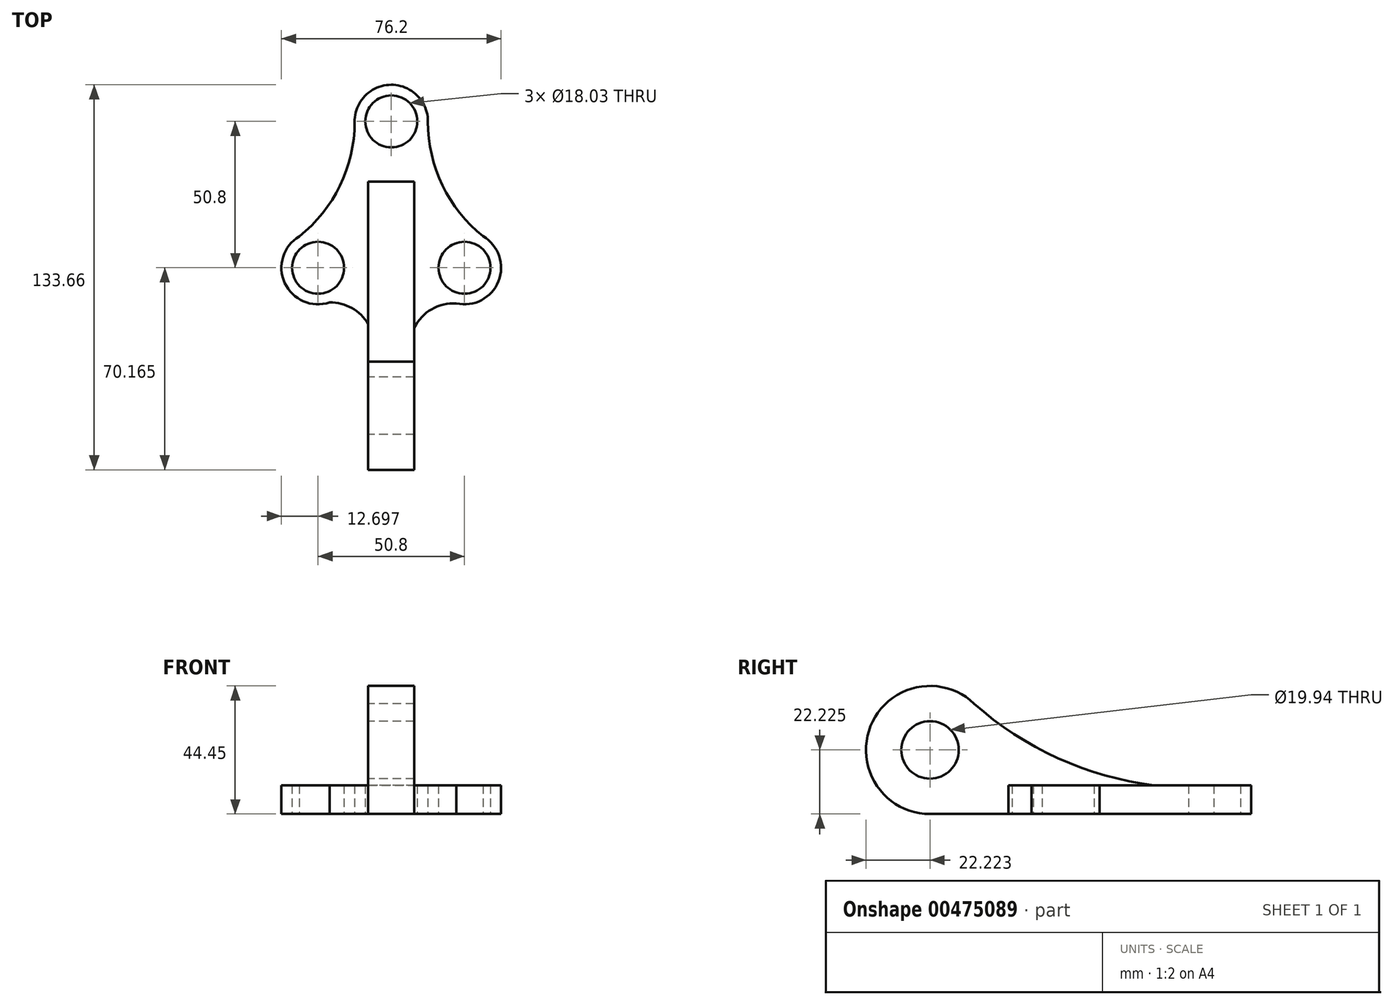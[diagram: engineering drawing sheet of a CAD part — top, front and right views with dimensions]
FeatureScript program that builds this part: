
annotation { "Feature Type Name" : "Feature", "Feature Type Description" : "" }
export const myFeature = defineFeature(function(context is Context, id is Id, definition is map)
    precondition{}
    {
        {
            var Q0;
            Q0=qCreatedBy(makeId("Top.planeOp"),FACE);
            var sketch = newSketch(context, id + "F0", { "sketchPlane" : qUnion([Q0])});
            skCircle(sketch, "E0", {"center": v(-223.53, 109.86) * mm, "radius": 12.7 * mm});
            skCircle(sketch, "E1", {"center": v(-248.93, 59.06) * mm, "radius": 12.7 * mm});
            skCircle(sketch, "E2", {"center": v(-198.13, 59.06) * mm, "radius": 12.7 * mm});
            skPoint(sketch, "E3", {"position": v(-236.23, 110.12) * mm});
            skPoint(sketch, "E4", {"position": v(-210.83, 109.93) * mm});
            skPoint(sketch, "E5", {"position": v(-191.66, 69.98) * mm});
            skArc(sketch, "E6", {"start": v(-210.83, 109.93) * mm, "mid": v(-205.83, 87.76) * mm, "end": v(-191.66, 69.98) * mm});
            skLineSegment(sketch, "E7.bottom", {"start": v(-231.53, 88.9) * mm, "end": v(-215.53, 88.9) * mm});
            skLineSegment(sketch, "E7.top", {"start": v(-231.53, 0) * mm, "end": v(-215.53, 0) * mm});
            skLineSegment(sketch, "E7.left", {"start": v(-231.53, 88.9) * mm, "end": v(-231.53, 0) * mm});
            skLineSegment(sketch, "E7.right", {"start": v(-215.53, 88.9) * mm, "end": v(-215.53, 0) * mm});
            skCircle(sketch, "E8", {"center": v(-248.93, 59.06) * mm, "radius": 9.02 * mm});
            skCircle(sketch, "E9", {"center": v(-198.13, 59.06) * mm, "radius": 9.02 * mm});
            skCircle(sketch, "E10", {"center": v(-223.53, 109.86) * mm, "radius": 9.02 * mm});
            skPoint(sketch, "E11", {"position": v(-257.57, 68.36) * mm});
            skArc(sketch, "E12", {"start": v(-257.57, 68.36) * mm, "mid": v(-241.8, 86.63) * mm, "end": v(-236.23, 110.12) * mm});
            skPoint(sketch, "E13", {"position": v(-198.74, 46.37) * mm});
            skPoint(sketch, "E14", {"position": v(-215.53, 38.26) * mm});
            skPoint(sketch, "E15", {"position": v(-231.53, 39.54) * mm});
            skArc(sketch, "E16", {"start": v(-198.74, 46.37) * mm, "mid": v(-208.52, 45.19) * mm, "end": v(-215.53, 38.26) * mm});
            skPoint(sketch, "E17", {"position": v(-249.02, 46.36) * mm});
            skArc(sketch, "E18", {"start": v(-231.53, 39.54) * mm, "mid": v(-239.1, 45.96) * mm, "end": v(-249.02, 46.36) * mm});
            skLineSegment(sketch, "E19.top", {"start": v(-231.53, -11.11) * mm, "end": v(-215.53, -11.11) * mm});
            skLineSegment(sketch, "E19.left", {"start": v(-231.53, 0) * mm, "end": v(-231.53, -11.11) * mm});
            skLineSegment(sketch, "E19.right", {"start": v(-215.53, 0) * mm, "end": v(-215.53, -11.11) * mm});
            skSolve(sketch);
        }
        {
            var Q0;
            {var subQ3=sQuery(id+"F0.wireOp",EDGE,"E7.bottom");Q0=makeQuery(id+"F0.imprint","IMPRINT",FACE,{"disambiguationData":[TD([[makeQuery(id+"F0.imprint","IMPRINT",EDGE,{"derivedFrom":subQ3}),-1.0]])]});}
            var Q1;
            Q1=makeQuery(id+"F0.imprint","IMPRINT",FACE,{"disambiguationData":[TD([[makeQuery(id+"F0.imprint","IMPRINT",EDGE,{"derivedFrom":sQuery(id+"F0.wireOp",EDGE,"E7.top")}),-1.0]])]});
            extrude(context, id + "F1", {"entities" : qUnion([Q0, Q1]), "depth" : 76.2 * mm});
        }
        {
            var Q0;
            Q0 = qSketchRegion(id + "F0", true);
            extrude(context, id + "F2", {"entities" : qUnion([Q0]), "operationType" : NewBodyOperationType.ADD, "depth" : 10 * mm});
        }
        {
            var Q0;
            Q0=makeQuery(id+"F1.opExtrude","SWEPT_FACE",FACE,{"disambiguationData":[OSD([sQuery(id+"F0.wireOp",EDGE,"E7.left")])]});
            var sketch = newSketch(context, id + "F3", { "sketchPlane" : qUnion([Q0])});
            skCircle(sketch, "E20", {"center": v(-11.11, 22.23) * mm, "radius": 22.23 * mm});
            skPoint(sketch, "E21", {"position": v(11.11, 38.1) * mm});
            skLineSegment(sketch, "E22", {"start": v(-39.54, 0) * mm, "end": v(0, 0) * mm});
            skLineSegment(sketch, "E23", {"start": v(0, 0) * mm, "end": v(-39.54, 0) * mm});
            skCircle(sketch, "E24", {"center": v(-11.11, 22.23) * mm, "radius": 9.97 * mm});
            skArc(sketch, "E25", {"start": v(-88.9, 10) * mm, "mid": v(-55.5, 19.37) * mm, "end": v(-26.43, 38.33) * mm});
            skSolve(sketch);
        }
        {
            var Q0;
            {var subQ0=sQuery(id+"F0.wireOp",EDGE,"E7.left");var subQ2=sQuery(id+"F0.wireOp",EDGE,"E19.left");var subQ3=makeQuery(id+"F1.opExtrude","CAP_EDGE",EDGE,{"disambiguationData":[OSD([subQ0,subQ2])],"isStart":false});Q0=makeQuery(id+"F3.imprint","IMPRINT",FACE,{"disambiguationData":[TD([[makeQuery(id+"F3.imprint","IMPRINT",EDGE,{"derivedFrom":subQ3}),-1.0]])]});}
            var Q1;
            Q1=makeQuery(id+"F3.imprint","IMPRINT",FACE,{"disambiguationData":[TD([[makeQuery(id+"F3.imprint","IMPRINT",EDGE,{"derivedFrom":sQuery(id+"F3.wireOp",EDGE,"E24")}),1.0]])]});
            var Q2;
            {var subQ0=sQuery(id+"F3.wireOp",EDGE,"E23");var subQ1=sQuery(id+"F3.wireOp",EDGE,"E20");var subQ2=makeQuery(id+"F3.imprint","INTERSECT",VERTEX,{"derivedFrom":[subQ1,subQ0]});Q2=makeQuery(id+"F3.imprint","IMPRINT",FACE,{"disambiguationData":[TD([[makeQuery(id+"F3.imprint","IMPRINT",EDGE,{"disambiguationData":[TD([[subQ2,-1.0]])],"derivedFrom":subQ1}),-1.0]])]});}
            var Q3;
            {var subQ0=sQuery(id+"F3.wireOp",EDGE,"ZB10SysG-g3e0-j2N3-KAlu-umGnWbLpoUqT");var subQ1=sQuery(id+"F3.wireOp",EDGE,"E20");var subQ2=makeQuery(id+"F3.imprint","INTERSECT",VERTEX,{"derivedFrom":[subQ1,subQ0]});Q3=makeQuery(id+"F3.imprint","IMPRINT",FACE,{"disambiguationData":[TD([[makeQuery(id+"F3.imprint","IMPRINT",EDGE,{"disambiguationData":[TD([[subQ2,1.0]])],"derivedFrom":subQ1}),-1.0]])]});}
            extrude(context, id + "F4", {"entities" : qUnion([Q0, Q1, Q2, Q3]), "operationType" : NewBodyOperationType.REMOVE, "oppositeDirection" : true, "depth" : 25.4 * mm});
        }
    });
